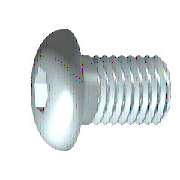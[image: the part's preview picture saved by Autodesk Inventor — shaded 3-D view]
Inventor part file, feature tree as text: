
AUTODESK INVENTOR PART (.ipt)
format: ipt  version: 2015 (Build 190159000, 159)  size: 200,192 bytes
history: native  units: mm (DEFAULTED — no unit token found)
features: sketch x2, extrude x1, plane x1, fillet x1
ambient origin geometry x7: Origin, YZ Plane, XY Plane, X Axis, Y Axis, Z Axis, Center Point
bodies: Solid1 (feature_tree), Body (feature_tree)
feature tree (5):
  extrude  "Slot"  Depth=3.3528mm
  plane  "Work Plane1"
  fillet  "Fillet2"  Radius=3.3528mm
  sketch  "Sketch1"  dims[d1=10.1598mm d2=2.5401mm d3=3.3528mm]
  sketch  "Sketch2"  dims[d4=2.2098mm d5=60.0deg d6=6.35mm d7=6.35mm d8=4.575385mm d9=11.0998mm d10=90.0deg d11=10.0mm d12=0.0mm d13=10.1598mm d14=0.0mm d15=0.779018mm d16=0.779018mm d17=2.9718mm d19=0.0mm d26=12.7mm d27=45.0deg d28=0.0mm d29=0.0mm d30=0.1mm]
